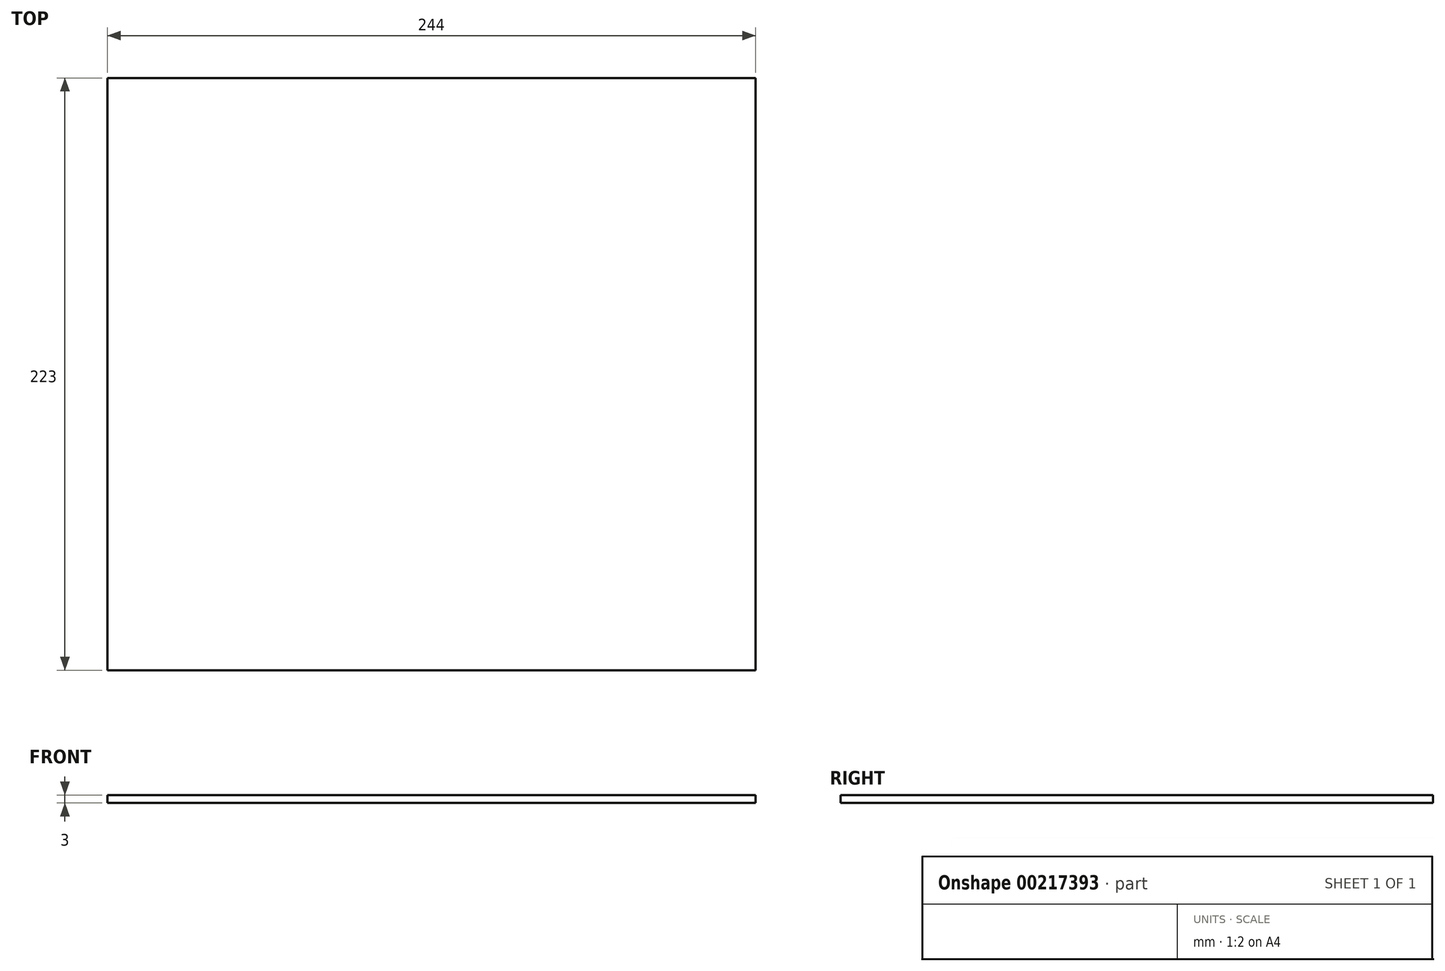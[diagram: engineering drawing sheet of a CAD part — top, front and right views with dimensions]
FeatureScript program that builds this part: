
annotation { "Feature Type Name" : "Feature", "Feature Type Description" : "" }
export const myFeature = defineFeature(function(context is Context, id is Id, definition is map)
    precondition{}
    {
        {
            var Q0;
            Q0=qCreatedBy(makeId("Top.planeOp"),FACE);
            var sketch = newSketch(context, id + "F0", { "sketchPlane" : qUnion([Q0])});
            skLineSegment(sketch, "E0.bottom", {"start": v(-132.68, -166.4) * mm, "end": v(111.32, -166.4) * mm});
            skLineSegment(sketch, "E0.top", {"start": v(-132.68, 56.6) * mm, "end": v(111.32, 56.6) * mm});
            skLineSegment(sketch, "E0.left", {"start": v(-132.68, -166.4) * mm, "end": v(-132.68, 56.6) * mm});
            skLineSegment(sketch, "E0.right", {"start": v(111.32, -166.4) * mm, "end": v(111.32, 56.6) * mm});
            skSolve(sketch);
        }
        {
            var Q0;
            Q0=makeQuery(id+"F0.imprint","IMPRINT",FACE,{"disambiguationData":[TD([[makeQuery(id+"F0.imprint","IMPRINT",EDGE,{"derivedFrom":sQuery(id+"F0.wireOp",EDGE,"E0.bottom")}),1.0]])]});
            extrude(context, id + "F1", {"entities" : qUnion([Q0]), "depth" : 3 * mm});
        }
    });
